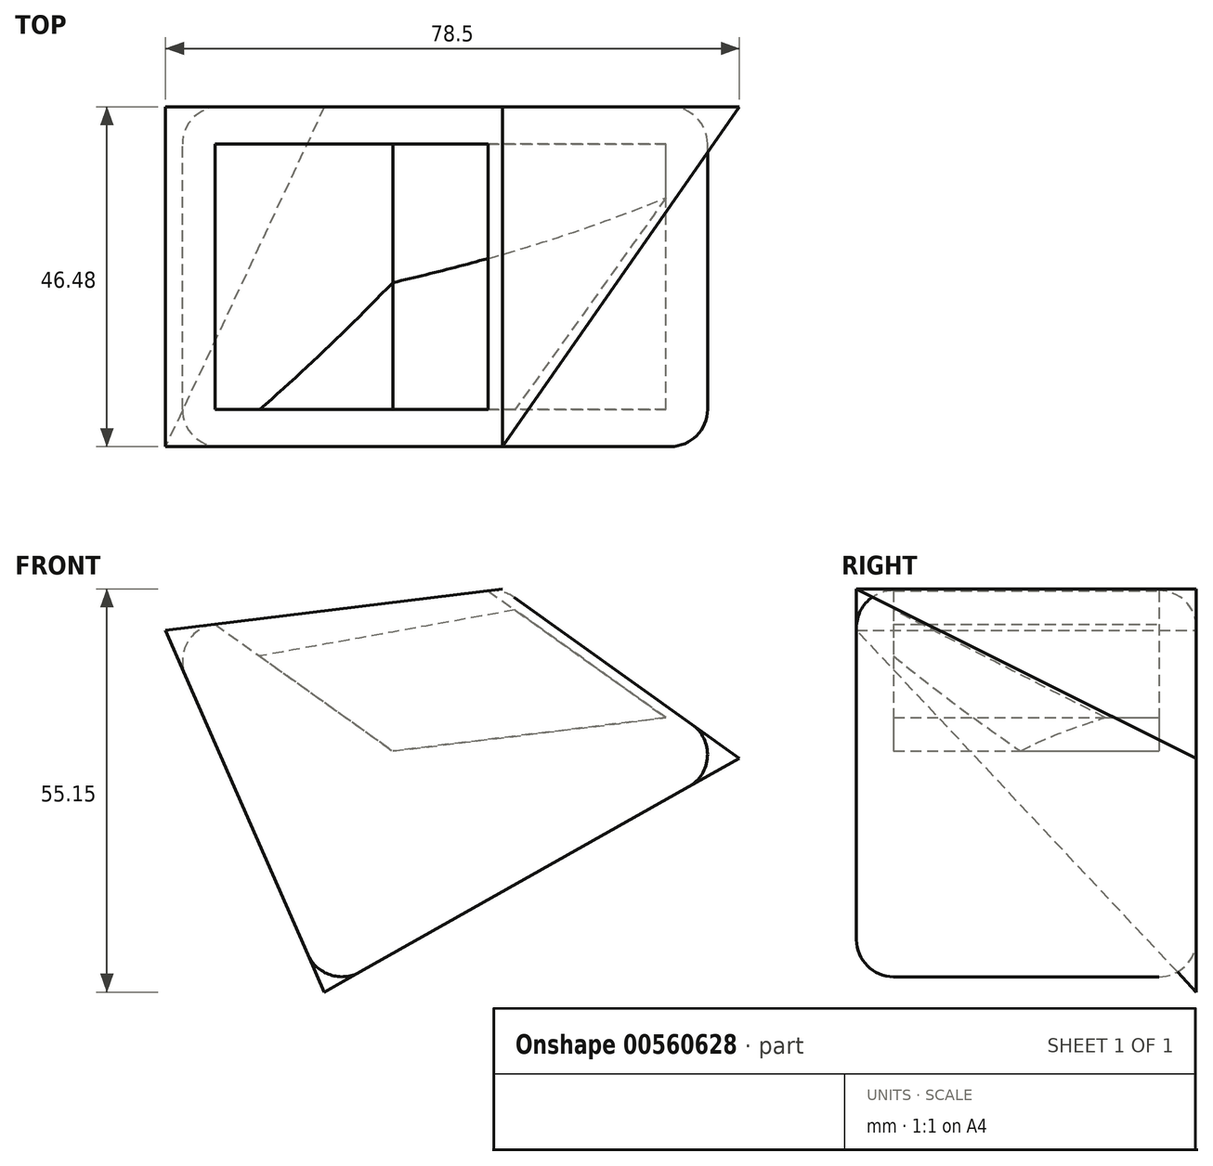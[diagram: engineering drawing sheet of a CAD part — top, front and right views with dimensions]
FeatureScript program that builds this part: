
annotation { "Feature Type Name" : "Feature", "Feature Type Description" : "" }
export const myFeature = defineFeature(function(context is Context, id is Id, definition is map)
    precondition{}
    {
        {
            var Q0;
            Q0=qCreatedBy(makeId("Front.planeOp"),FACE);
            var sketch = newSketch(context, id + "F0", { "sketchPlane" : qUnion([Q0])});
            skLineSegment(sketch, "E0", {"start": v(-48.91, 45.8) * mm, "end": v(-27.17, -3.72) * mm});
            skLineSegment(sketch, "E1", {"start": v(-27.17, -3.72) * mm, "end": v(29.59, 28.28) * mm});
            skLineSegment(sketch, "E2", {"start": v(29.59, 28.28) * mm, "end": v(-2.82, 51.43) * mm});
            skLineSegment(sketch, "E3", {"start": v(-2.82, 51.43) * mm, "end": v(-48.91, 45.8) * mm});
            skSolve(sketch);
        }
        {
            var Q0;
            Q0 = qSketchRegion(id + "F0", true);
            extrude(context, id + "F1", {"entities" : qUnion([Q0]), "depth" : 46.48 * mm, "offsetDistance" : 25.4 * mm});
        }
        {
            var Q0;
            Q0=makeQuery(id+"F1.opExtrude","CAP_FACE",FACE,{"disambiguationData":[OSD([sQuery(id+"F0.wireOp",EDGE,"E0"),sQuery(id+"F0.wireOp",EDGE,"E1"),sQuery(id+"F0.wireOp",EDGE,"E2"),sQuery(id+"F0.wireOp",EDGE,"E3")])],"isStart":true});
            var Q1;
            Q1=makeQuery(id+"F1.opExtrude","SWEPT_FACE",FACE,{"disambiguationData":[OSD([sQuery(id+"F0.wireOp",EDGE,"E3")])]});
            loft(context, id + "F2", {"sheetProfilesArray" : [{ "sheetProfileEntities" : qUnion([Q0]) }, { "sheetProfileEntities" : qUnion([Q1]) }]});
        }
        {
            var Q0;
            Q0=makeQuery(id+"F1.opExtrude","SWEPT_FACE",FACE,{"disambiguationData":[OSD([sQuery(id+"F0.wireOp",EDGE,"E3")])]});
            var Q1;
            Q1=makeQuery(id+"F1.opExtrude","CAP_FACE",FACE,{"disambiguationData":[OSD([sQuery(id+"F0.wireOp",EDGE,"E0"),sQuery(id+"F0.wireOp",EDGE,"E1"),sQuery(id+"F0.wireOp",EDGE,"E2"),sQuery(id+"F0.wireOp",EDGE,"E3")])],"isStart":true});
            var Q2;
            Q2=makeQuery(id+"F1.opExtrude","SWEPT_FACE",FACE,{"disambiguationData":[OSD([sQuery(id+"F0.wireOp",EDGE,"E1")])]});
            var Q3;
            Q3=makeQuery(id+"F1.opExtrude","CAP_EDGE",EDGE,{"disambiguationData":[OSD([sQuery(id+"F0.wireOp",EDGE,"E3")])],"isStart":true});
            var Q4;
            Q4=makeQuery(id+"F1.opExtrude","CAP_EDGE",EDGE,{"disambiguationData":[OSD([sQuery(id+"F0.wireOp",EDGE,"E1")])],"isStart":true});
            var Q5;
            Q5=makeQuery(id+"F1.opExtrude","SWEPT_FACE",FACE,{"disambiguationData":[OSD([sQuery(id+"F0.wireOp",EDGE,"E0")])]});
            var Q6;
            Q6=makeQuery(id+"F1.opExtrude","CAP_FACE",FACE,{"disambiguationData":[OSD([sQuery(id+"F0.wireOp",EDGE,"E0"),sQuery(id+"F0.wireOp",EDGE,"E1"),sQuery(id+"F0.wireOp",EDGE,"E2"),sQuery(id+"F0.wireOp",EDGE,"E3")])],"isStart":false});
            fillet(context, id + "F3", {"entities" : qUnion([Q0, Q1, Q2, Q3, Q4, Q5, Q6]), "radius" : 5.08 * mm, "tangentPropagation" : true, "allowEdgeOverflow" : false});
        }
        {
            var Q0;
            Q0=makeQuery(id+"F1.opExtrude","SWEPT_FACE",FACE,{"disambiguationData":[OSD([sQuery(id+"F0.wireOp",EDGE,"E3")])]});
            var Q1;
            {var subQ0=sQuery(id+"F0.wireOp",EDGE,"E2");Q1=makeQuery(id+"F3.opFillet","BLEND_EDGE",EDGE,{"blendedFrom":[makeQuery(id+"F1.opExtrude","CAP_EDGE",EDGE,{"disambiguationData":[OSD([subQ0])],"isStart":false}),makeQuery(id+"F1.opExtrude","SWEPT_FACE",FACE,{"disambiguationData":[OSD([subQ0])]})],"blendedInto":[makeQuery(id+"F1.opExtrude","SWEPT_FACE",FACE,{"disambiguationData":[OSD([subQ0])]})]});}
            sweep(context, id + "F4", {"operationType" : NewBodyOperationType.REMOVE, "profiles" : qUnion([Q0]), "path" : qUnion([Q1])});
        }
    });
